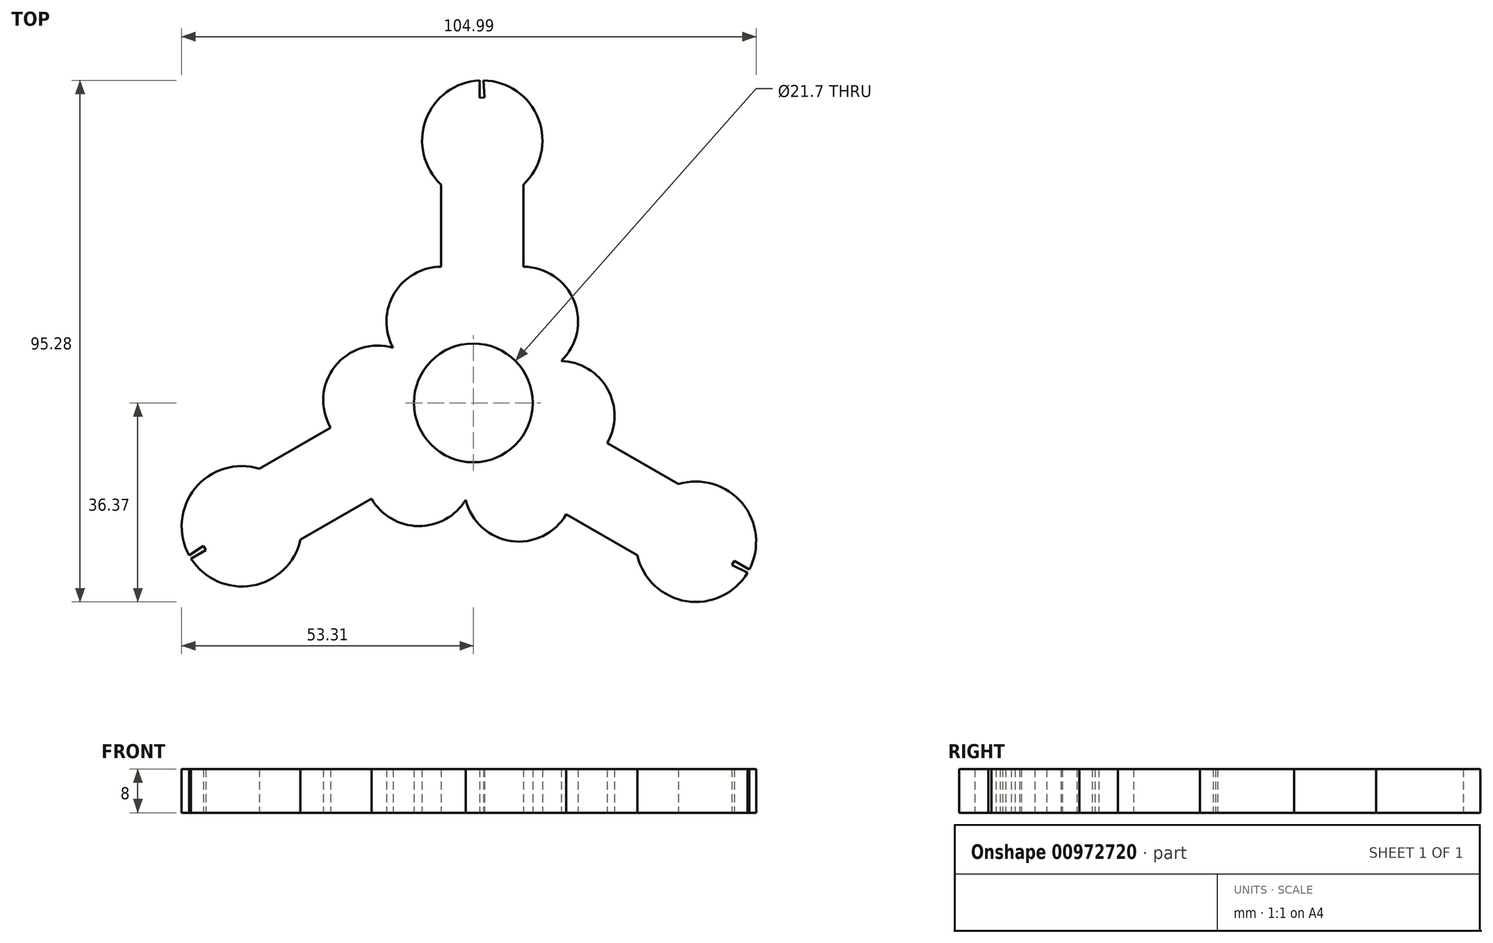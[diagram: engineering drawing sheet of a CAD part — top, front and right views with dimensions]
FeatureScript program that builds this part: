
annotation { "Feature Type Name" : "Feature", "Feature Type Description" : "" }
export const myFeature = defineFeature(function(context is Context, id is Id, definition is map)
    precondition{}
    {
        {
            var Q0;
            Q0=qCreatedBy(makeId("Top.planeOp"),FACE);
            var sketch = newSketch(context, id + "F0", { "sketchPlane" : qUnion([Q0])});
            skArc(sketch, "E0", {"start": v(9.13, 39.86) * mm, "mid": v(11.9, 51.84) * mm, "end": v(1.84, 58.9) * mm});
            skLineSegment(sketch, "E1", {"start": v(-5.87, 39.86) * mm, "end": v(-5.87, 24.86) * mm});
            skLineSegment(sketch, "E2", {"start": v(9.13, 39.86) * mm, "end": v(9.13, 24.86) * mm});
            skArc(sketch, "E3", {"start": v(-5.87, 24.86) * mm, "mid": v(-14.47, 19.97) * mm, "end": v(-14.65, 10.08) * mm});
            skPoint(sketch, "E4.orphan", {"position": v(-5.87, 24.86) * mm});
            skPoint(sketch, "E5.orphan", {"position": v(9.13, 14.86) * mm});
            skLineSegment(sketch, "E6.left", {"start": v(1.84, 58.9) * mm, "end": v(2.03, 55.76) * mm});
            skArc(sketch, "E7.trimOffspring", {"start": v(1.16, 58.9) * mm, "mid": v(-8.69, 51.72) * mm, "end": v(-5.87, 39.86) * mm});
            skPoint(sketch, "E8.center.orphan", {"position": v(1.63, 4.12) * mm});
            skLineSegment(sketch, "E9", {"start": v(1.16, 58.9) * mm, "end": v(1.16, 55.75) * mm});
            skLineSegment(sketch, "E10", {"start": v(2.03, 55.76) * mm, "end": v(1.16, 55.75) * mm});
            skLineSegment(sketch, "E11.1.1", {"start": v(37.46, -14.85) * mm, "end": v(24.47, -7.35) * mm});
            skPoint(sketch, "E11.1.2", {"position": v(8.3, -15.34) * mm});
            skArc(sketch, "E11.1.3", {"start": v(29.96, -27.84) * mm, "mid": v(38.94, -36.23) * mm, "end": v(50.1, -31.05) * mm});
            skPoint(sketch, "E11.1.4", {"position": v(24.47, -7.35) * mm});
            skLineSegment(sketch, "E11.1.5", {"start": v(29.96, -27.84) * mm, "end": v(16.97, -20.34) * mm});
            skArc(sketch, "E11.1.6", {"start": v(24.47, -7.35) * mm, "mid": v(24.53, 2.54) * mm, "end": v(16.06, 7.65) * mm});
            skPoint(sketch, "E11.1.7", {"position": v(2.75, -3.47) * mm});
            skArc(sketch, "E11.1.8", {"start": v(50.43, -30.45) * mm, "mid": v(49.13, -18.34) * mm, "end": v(37.46, -14.85) * mm});
            skLineSegment(sketch, "E11.1.9", {"start": v(47.28, -29.63) * mm, "end": v(47.7, -28.88) * mm});
            skLineSegment(sketch, "E11.1.10", {"start": v(50.43, -30.45) * mm, "end": v(47.7, -28.88) * mm});
            skLineSegment(sketch, "E11.1.11", {"start": v(50.1, -31.05) * mm, "end": v(47.28, -29.63) * mm});
            skLineSegment(sketch, "E11.2.1", {"start": v(-31.59, -25.01) * mm, "end": v(-18.6, -17.51) * mm});
            skPoint(sketch, "E11.2.2", {"position": v(-17.44, 0.48) * mm});
            skArc(sketch, "E11.2.3", {"start": v(-39.09, -12.02) * mm, "mid": v(-50.85, -15.61) * mm, "end": v(-51.94, -27.86) * mm});
            skPoint(sketch, "E11.2.4", {"position": v(-18.6, -17.51) * mm});
            skLineSegment(sketch, "E11.2.5", {"start": v(-39.09, -12.02) * mm, "end": v(-26.1, -4.52) * mm});
            skArc(sketch, "E11.2.6", {"start": v(-18.6, -17.51) * mm, "mid": v(-10.06, -22.51) * mm, "end": v(-1.4, -17.73) * mm});
            skPoint(sketch, "E11.2.7", {"position": v(-4.38, -0.65) * mm});
            skArc(sketch, "E11.2.8", {"start": v(-51.59, -28.45) * mm, "mid": v(-40.45, -33.38) * mm, "end": v(-31.59, -25.01) * mm});
            skLineSegment(sketch, "E11.2.9", {"start": v(-49.3, -26.13) * mm, "end": v(-48.86, -26.87) * mm});
            skLineSegment(sketch, "E11.2.10", {"start": v(-51.59, -28.45) * mm, "end": v(-48.86, -26.87) * mm});
            skLineSegment(sketch, "E11.2.11", {"start": v(-51.94, -27.86) * mm, "end": v(-49.3, -26.13) * mm});
            skPoint(sketch, "E11.center", {"position": v(0, 0) * mm});
            skArc(sketch, "E12.trimOffspring", {"start": v(-14.65, 10.08) * mm, "mid": v(-25.3, 6.65) * mm, "end": v(-26.1, -4.52) * mm});
            skArc(sketch, "E13.trimOffspring", {"start": v(16.06, 7.65) * mm, "mid": v(18.4, 18.6) * mm, "end": v(9.13, 24.86) * mm});
            skArc(sketch, "E14.trimOffspring", {"start": v(-1.4, -17.73) * mm, "mid": v(6.9, -25.24) * mm, "end": v(16.97, -20.34) * mm});
            skPoint(sketch, "E15.orphan", {"position": v(1.63, 8.25) * mm});
            skPoint(sketch, "E16.orphan", {"position": v(-7.96, -2.71) * mm});
            skPoint(sketch, "E17.orphan", {"position": v(6.33, -5.54) * mm});
            skCircle(sketch, "E18", {"center": v(0, 0) * mm, "radius": 10.85 * mm});
            skSolve(sketch);
        }
        {
            var Q0;
            Q0=makeQuery(id+"F0.imprint","IMPRINT",FACE,{"disambiguationData":[TD([[makeQuery(id+"F0.imprint","IMPRINT",EDGE,{"derivedFrom":sQuery(id+"F0.wireOp",EDGE,"E0")}),1.0]])]});
            extrude(context, id + "F1", {"entities" : qUnion([Q0]), "depth" : 8 * mm, "offsetDistance" : 25 * mm});
        }
    });
